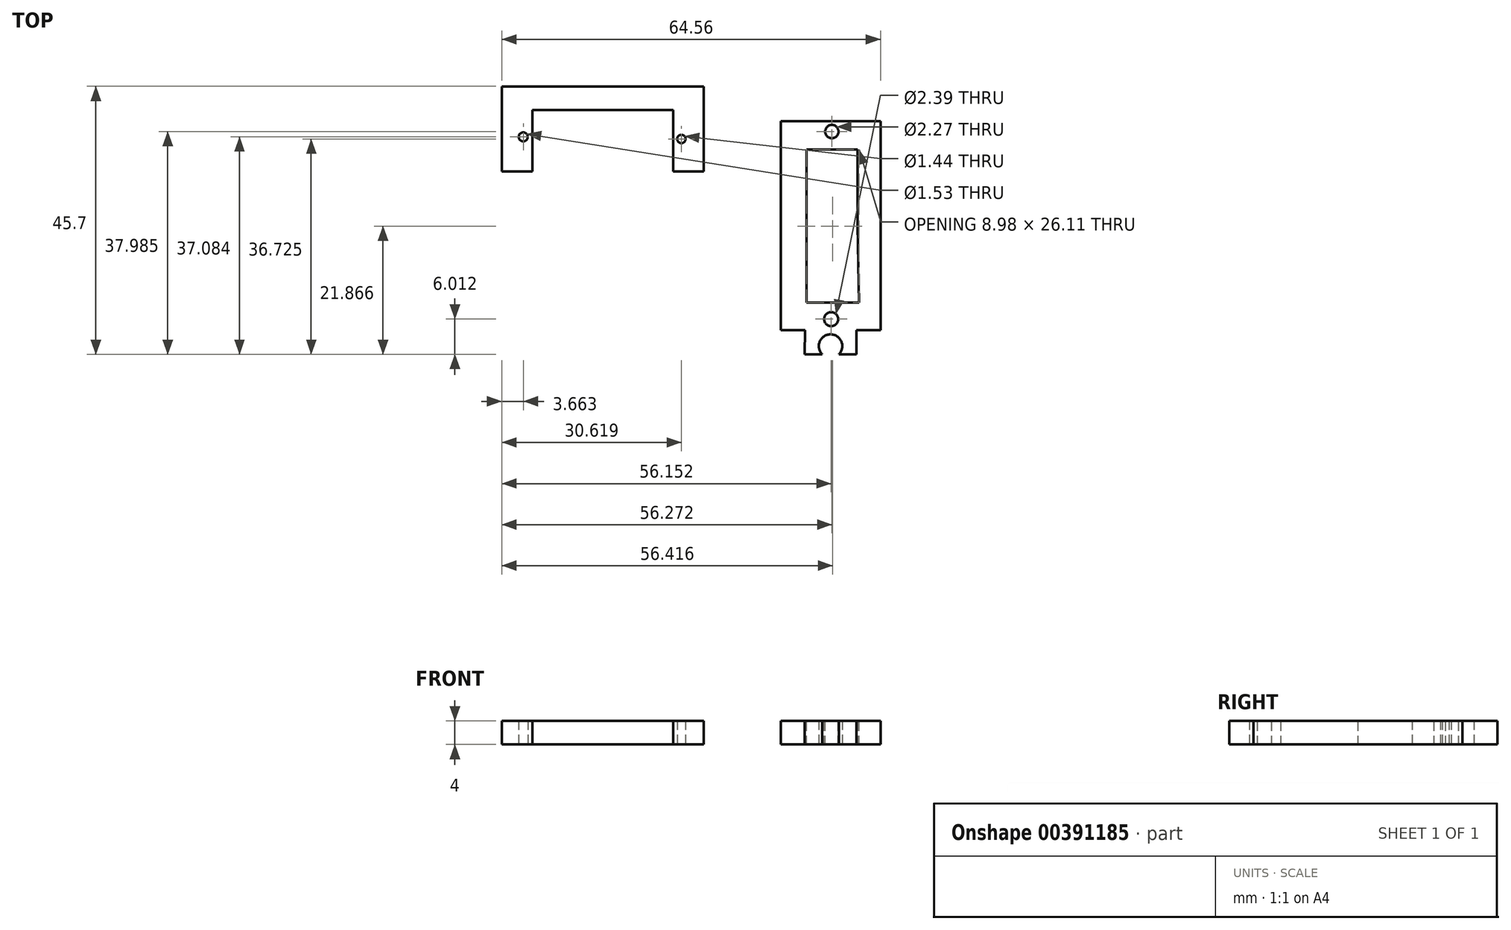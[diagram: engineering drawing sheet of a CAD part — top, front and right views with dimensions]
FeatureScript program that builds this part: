
annotation { "Feature Type Name" : "Feature", "Feature Type Description" : "" }
export const myFeature = defineFeature(function(context is Context, id is Id, definition is map)
    precondition{}
    {
        {
            var Q0;
            Q0=qCreatedBy(makeId("Top.planeOp"),FACE);
            var sketch = newSketch(context, id + "F0", { "sketchPlane" : qUnion([Q0])});
            skLineSegment(sketch, "E0", {"start": v(-47.56, 5.97) * mm, "end": v(-13.1, 5.97) * mm});
            skLineSegment(sketch, "E1", {"start": v(-13.1, 5.97) * mm, "end": v(-13.1, -8.53) * mm});
            skLineSegment(sketch, "E2", {"start": v(-13.1, -8.53) * mm, "end": v(-18.33, -8.53) * mm});
            skLineSegment(sketch, "E3", {"start": v(-18.33, -8.53) * mm, "end": v(-18.33, 1.97) * mm});
            skLineSegment(sketch, "E4", {"start": v(-47.56, 5.97) * mm, "end": v(-47.56, -8.53) * mm});
            skLineSegment(sketch, "E5", {"start": v(-47.56, -8.53) * mm, "end": v(-42.33, -8.53) * mm});
            skLineSegment(sketch, "E6", {"start": v(-42.33, -8.53) * mm, "end": v(-42.33, 1.97) * mm});
            skLineSegment(sketch, "E7", {"start": v(-42.33, 1.97) * mm, "end": v(-18.33, 1.97) * mm});
            skSolve(sketch);
        }
        {
            var Q0;
            Q0=qCreatedBy(makeId("Top.planeOp"),FACE);
            var sketch = newSketch(context, id + "F1", { "sketchPlane" : qUnion([Q0])});
            skCircle(sketch, "E8", {"center": v(-16.94, -3) * mm, "radius": 0.72 * mm});
            skCircle(sketch, "E9", {"center": v(-43.9, -2.65) * mm, "radius": 0.77 * mm});
            skSolve(sketch);
        }
        {
            var Q0;
            Q0=makeQuery(id+"F0.imprint","IMPRINT",FACE,{"disambiguationData":[TD([[makeQuery(id+"F0.imprint","IMPRINT",EDGE,{"derivedFrom":sQuery(id+"F0.wireOp",EDGE,"E0")}),-1.0]])]});
            extrude(context, id + "F2", {"entities" : qUnion([Q0]), "depth" : 4 * mm});
        }
        {
            var Q0;
            Q0=makeQuery(id+"F1.imprint","IMPRINT",FACE,{"disambiguationData":[TD([[makeQuery(id+"F1.imprint","IMPRINT",EDGE,{"derivedFrom":sQuery(id+"F1.wireOp",EDGE,"E8")}),1.0]])]});
            extrude(context, id + "F3", {"entities" : qUnion([Q0]), "operationType" : NewBodyOperationType.REMOVE, "depth" : 15.1 * mm});
        }
        {
            var Q0;
            Q0=makeQuery(id+"F1.imprint","IMPRINT",FACE,{"disambiguationData":[TD([[makeQuery(id+"F1.imprint","IMPRINT",EDGE,{"derivedFrom":sQuery(id+"F1.wireOp",EDGE,"E9")}),1.0]])]});
            extrude(context, id + "F4", {"entities" : qUnion([Q0]), "operationType" : NewBodyOperationType.REMOVE, "depth" : 25 * mm});
        }
        {
            var Q0;
            Q0=qCreatedBy(makeId("Top.planeOp"),FACE);
            var sketch = newSketch(context, id + "F5", { "sketchPlane" : qUnion([Q0])});
            skLineSegment(sketch, "E10", {"start": v(0, 0) * mm, "end": v(17, 0) * mm});
            skLineSegment(sketch, "E11", {"start": v(17, 0) * mm, "end": v(17, -35.61) * mm});
            skLineSegment(sketch, "E12", {"start": v(17, -35.61) * mm, "end": v(12.89, -35.61) * mm});
            skLineSegment(sketch, "E13", {"start": v(12.89, -35.61) * mm, "end": v(12.89, -39.73) * mm});
            skLineSegment(sketch, "E14", {"start": v(0, 0) * mm, "end": v(8.5, 0) * mm});
            skPoint(sketch, "E15.endSnap0", {"position": v(8.5, 0) * mm});
            skLineSegment(sketch, "E16.MirrorCS", {"start": v(17, 0) * mm, "end": v(0, 0) * mm});
            skLineSegment(sketch, "E17.MirrorCS", {"start": v(0, 0) * mm, "end": v(0, -35.61) * mm});
            skLineSegment(sketch, "E18.MirrorCS", {"start": v(0, -35.61) * mm, "end": v(4.11, -35.61) * mm});
            skLineSegment(sketch, "E19.MirrorCS", {"start": v(4.11, -35.61) * mm, "end": v(4.09, -39.73) * mm});
            skLineSegment(sketch, "E20", {"start": v(4.09, -39.73) * mm, "end": v(12.89, -39.73) * mm});
            skCircle(sketch, "E21", {"center": v(8.49, -38.31) * mm, "radius": 2 * mm});
            skPoint(sketch, "E21.centerSnap0", {"position": v(8.49, -39.73) * mm});
            skSolve(sketch);
        }
        {
            var Q0;
            {var subQ1=sQuery(id+"F5.wireOp",EDGE,"E11");Q0=makeQuery(id+"F5.imprint","IMPRINT",FACE,{"disambiguationData":[TD([[makeQuery(id+"F5.imprint","IMPRINT",EDGE,{"derivedFrom":subQ1}),-1.0]])]});}
            extrude(context, id + "F6", {"entities" : qUnion([Q0]), "depth" : 4 * mm});
        }
        {
            var Q0;
            Q0=makeQuery(id+"F6.opExtrude","CAP_FACE",FACE,{"disambiguationData":[OSD([sQuery(id+"F5.wireOp",EDGE,"E11"),sQuery(id+"F5.wireOp",EDGE,"E12"),sQuery(id+"F5.wireOp",EDGE,"E13"),sQuery(id+"F5.wireOp",EDGE,"E16.MirrorCS"),sQuery(id+"F5.wireOp",EDGE,"E17.MirrorCS"),sQuery(id+"F5.wireOp",EDGE,"E18.MirrorCS"),sQuery(id+"F5.wireOp",EDGE,"E19.MirrorCS"),sQuery(id+"F5.wireOp",EDGE,"E20"),sQuery(id+"F5.wireOp",EDGE,"E21")])],"isStart":false});
            var sketch = newSketch(context, id + "F7", { "sketchPlane" : qUnion([Q0])});
            skSolve(sketch);
        }
        {
            var Q0;
            {var subQ1=makeQuery(id+"F6.opExtrude","CAP_EDGE",EDGE,{"disambiguationData":[OSD([sQuery(id+"F5.wireOp",EDGE,"E11")])],"isStart":false});Q0=makeQuery(id+"F7.imprint","IMPRINT",FACE,{"disambiguationData":[TD([[makeQuery(id+"F7.imprint","IMPRINT",EDGE,{"derivedFrom":subQ1}),-1.0]])]});}
            var sketch = newSketch(context, id + "F8", { "sketchPlane" : qUnion([Q0])});
            skSolve(sketch);
        }
        {
            var Q0;
            {var subQ1=makeQuery(id+"F6.opExtrude","CAP_EDGE",EDGE,{"disambiguationData":[OSD([sQuery(id+"F5.wireOp",EDGE,"E11")])],"isStart":false});Q0=makeQuery(id+"F7.imprint","IMPRINT",FACE,{"disambiguationData":[TD([[makeQuery(id+"F7.imprint","IMPRINT",EDGE,{"derivedFrom":subQ1}),-1.0]])]});}
            var sketch = newSketch(context, id + "F9", { "sketchPlane" : qUnion([Q0])});
            skSolve(sketch);
        }
        {
            var Q0;
            {var subQ1=makeQuery(id+"F6.opExtrude","CAP_EDGE",EDGE,{"disambiguationData":[OSD([sQuery(id+"F5.wireOp",EDGE,"E11")])],"isStart":false});Q0=makeQuery(id+"F7.imprint","IMPRINT",FACE,{"disambiguationData":[TD([[makeQuery(id+"F7.imprint","IMPRINT",EDGE,{"derivedFrom":subQ1}),-1.0]])]});}
            var sketch = newSketch(context, id + "F10", { "sketchPlane" : qUnion([Q0])});
            skLineSegment(sketch, "E22.top", {"start": v(4.37, -4.81) * mm, "end": v(13.1, -4.81) * mm});
            skLineSegment(sketch, "E22.left", {"start": v(4.37, -17.74) * mm, "end": v(4.37, -4.81) * mm});
            skLineSegment(sketch, "E22.right", {"start": v(13.1, -17.74) * mm, "end": v(13.1, -4.81) * mm});
            skLineSegment(sketch, "E23", {"start": v(4.37, -17.74) * mm, "end": v(4.37, -30.92) * mm});
            skLineSegment(sketch, "E24", {"start": v(4.37, -30.92) * mm, "end": v(13.35, -30.92) * mm});
            skLineSegment(sketch, "E25", {"start": v(13.35, -30.92) * mm, "end": v(13.1, -17.74) * mm});
            skSolve(sketch);
        }
        {
            var Q0;
            Q0 = qSketchRegion(id + "F10", true);
            var Q1;
            Q1=makeQuery(id+"F7.imprint","IMPRINT",FACE,{"disambiguationData":[TD([[makeQuery(id+"F7.imprint","IMPRINT",EDGE,{"derivedFrom":makeQuery(id+"F6.opExtrude","CAP_EDGE",EDGE,{"disambiguationData":[OSD([sQuery(id+"F5.wireOp",EDGE,"E11")])],"isStart":false})}),-1.0]])]});
            extrude(context, id + "F11", {"entities" : qUnion([Q0, Q1]), "operationType" : NewBodyOperationType.ADD, "oppositeDirection" : true, "depth" : 4 * mm});
        }
        {
            var Q0;
            Q0 = qSketchRegion(id + "F10", true);
            extrude(context, id + "F12", {"entities" : qUnion([Q0]), "operationType" : NewBodyOperationType.REMOVE, "oppositeDirection" : true, "depth" : 25 * mm});
        }
        {
            var Q0;
            Q0=makeQuery(id+"F8.imprint","IMPRINT",FACE,{"disambiguationData":[TD([[makeQuery(id+"F8.imprint","IMPRINT",EDGE,{"derivedFrom":makeQuery(id+"F7.imprint","IMPRINT",EDGE,{"derivedFrom":makeQuery(id+"F6.opExtrude","CAP_EDGE",EDGE,{"disambiguationData":[OSD([sQuery(id+"F5.wireOp",EDGE,"E11")])],"isStart":false})})}),-1.0]])]});
            var sketch = newSketch(context, id + "F13", { "sketchPlane" : qUnion([Q0])});
            skCircle(sketch, "E26", {"center": v(8.82, -2.1) * mm, "radius": 1.03 * mm});
            skCircle(sketch, "E27", {"center": v(8.14, -33.43) * mm, "radius": 1.15 * mm});
            skSolve(sketch);
        }
        {
            var Q0;
            Q0=makeQuery(id+"F9.imprint","IMPRINT",FACE,{"disambiguationData":[TD([[makeQuery(id+"F9.imprint","IMPRINT",EDGE,{"derivedFrom":makeQuery(id+"F7.imprint","IMPRINT",EDGE,{"derivedFrom":makeQuery(id+"F6.opExtrude","CAP_EDGE",EDGE,{"disambiguationData":[OSD([sQuery(id+"F5.wireOp",EDGE,"E11")])],"isStart":false})})}),-1.0]])]});
            var sketch = newSketch(context, id + "F14", { "sketchPlane" : qUnion([Q0])});
            skCircle(sketch, "E28", {"center": v(8.38, -33.63) * mm, "radius": 1.39 * mm});
            skCircle(sketch, "E29", {"center": v(8.55, -2.05) * mm, "radius": 0.99 * mm});
            skSolve(sketch);
        }
        {
            var Q0;
            Q0=makeQuery(id+"F14.imprint","IMPRINT",FACE,{"disambiguationData":[TD([[makeQuery(id+"F14.imprint","IMPRINT",EDGE,{"derivedFrom":sQuery(id+"F14.wireOp",EDGE,"E29")}),1.0]])]});
            var Q1;
            Q1=sQuery(id+"F13.wireOp",EDGE,"E26");
            extrude(context, id + "F15", {"entities" : qUnion([Q0]), "operationType" : NewBodyOperationType.REMOVE, "surfaceEntities" : qUnion([Q1]), "depth" : 55.7 * mm});
        }
        {
            var Q0;
            Q0=makeQuery(id+"F9.imprint","IMPRINT",FACE,{"disambiguationData":[TD([[makeQuery(id+"F9.imprint","IMPRINT",EDGE,{"derivedFrom":makeQuery(id+"F7.imprint","IMPRINT",EDGE,{"derivedFrom":makeQuery(id+"F6.opExtrude","CAP_EDGE",EDGE,{"disambiguationData":[OSD([sQuery(id+"F5.wireOp",EDGE,"E11")])],"isStart":false})})}),-1.0]])]});
            var sketch = newSketch(context, id + "F16", { "sketchPlane" : qUnion([Q0])});
            skCircle(sketch, "E30", {"center": v(8.71, -1.74) * mm, "radius": 1.14 * mm});
            skCircle(sketch, "E31", {"center": v(8.6, -33.72) * mm, "radius": 1.2 * mm});
            skSolve(sketch);
        }
        {
            var Q0;
            Q0 = qSketchRegion(id + "F16", true);
            extrude(context, id + "F17", {"entities" : qUnion([Q0]), "operationType" : NewBodyOperationType.REMOVE, "oppositeDirection" : true, "depth" : 25 * mm});
        }
    });
